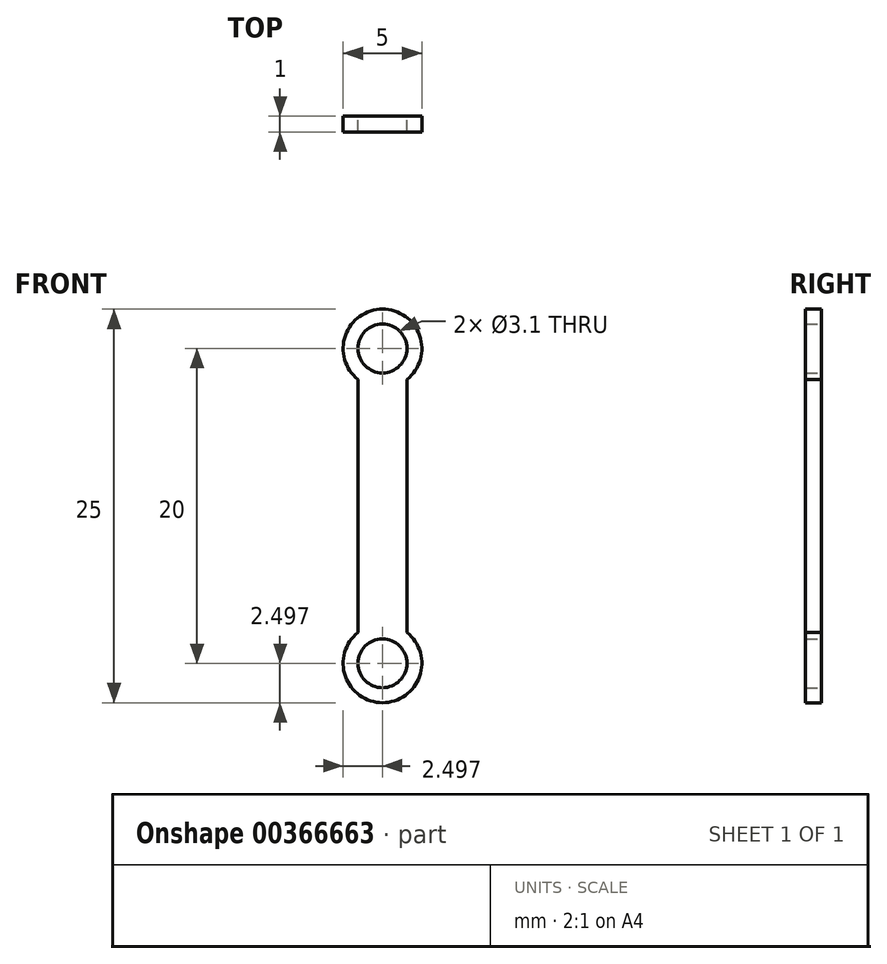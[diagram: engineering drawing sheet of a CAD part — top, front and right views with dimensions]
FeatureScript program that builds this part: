
annotation { "Feature Type Name" : "Feature", "Feature Type Description" : "" }
export const myFeature = defineFeature(function(context is Context, id is Id, definition is map)
    precondition{}
    {
        {
            var Q0;
            Q0=qCreatedBy(makeId("Front.planeOp"),FACE);
            var sketch = newSketch(context, id + "F0", { "sketchPlane" : qUnion([Q0])});
            skCircle(sketch, "E0", {"center": v(12.96, 10.03) * mm, "radius": 1.55 * mm});
            skCircle(sketch, "E1", {"center": v(12.96, 30.03) * mm, "radius": 1.55 * mm});
            skArc(sketch, "E2", {"start": v(14.5, 28.07) * mm, "mid": v(12.96, 32.53) * mm, "end": v(11.4, 28.07) * mm});
            skArc(sketch, "E3", {"start": v(11.4, 11.99) * mm, "mid": v(12.96, 7.53) * mm, "end": v(14.5, 11.99) * mm});
            skLineSegment(sketch, "E4", {"start": v(14.5, 28.07) * mm, "end": v(14.5, 11.99) * mm});
            skLineSegment(sketch, "E5", {"start": v(11.4, 28.07) * mm, "end": v(11.4, 11.99) * mm});
            skSolve(sketch);
        }
        {
            var Q0;
            Q0=makeQuery(id+"F0.imprint","IMPRINT",FACE,{"disambiguationData":[TD([[makeQuery(id+"F0.imprint","IMPRINT",EDGE,{"derivedFrom":sQuery(id+"F0.wireOp",EDGE,"E0")}),-1.0]])]});
            extrude(context, id + "F1", {"entities" : qUnion([Q0]), "depth" : 4.5 * mm});
        }
        {
            var Q0;
            Q0=makeQuery(id+"F1.opExtrude","SWEPT_FACE",FACE,{"disambiguationData":[OSD([sQuery(id+"F0.wireOp",EDGE,"E4")])]});
            var sketch = newSketch(context, id + "F2", { "sketchPlane" : qUnion([Q0])});
            skLineSegment(sketch, "E6.bottom", {"start": v(-1, 33.2) * mm, "end": v(-3.5, 33.2) * mm});
            skLineSegment(sketch, "E6.top", {"start": v(-1, 26.87) * mm, "end": v(-3.5, 26.87) * mm});
            skLineSegment(sketch, "E6.left", {"start": v(-1, 33.2) * mm, "end": v(-1, 26.87) * mm});
            skLineSegment(sketch, "E6.right", {"start": v(-3.5, 33.2) * mm, "end": v(-3.5, 26.87) * mm});
            skSolve(sketch);
        }
        {
            var Q0;
            Q0 = qSketchRegion(id + "F2", true);
            extrude(context, id + "F3", {"entities" : qUnion([Q0]), "operationType" : NewBodyOperationType.REMOVE, "endBound" : BoundingType.THROUGH_ALL, "oppositeDirection" : true, "depth" : 25 * mm, "hasSecondDirection" : true, "secondDirectionBound" : SecondDirectionBoundingType.THROUGH_ALL, "secondDirectionOppositeDirection" : false, "secondDirectionDepth" : 25 * mm});
        }
        {
            var Q0;
            Q0=makeQuery(id+"F1.opExtrude","CAP_FACE",FACE,{"disambiguationData":[OSD([sQuery(id+"F0.wireOp",EDGE,"E0"),sQuery(id+"F0.wireOp",EDGE,"E1"),sQuery(id+"F0.wireOp",EDGE,"E2"),sQuery(id+"F0.wireOp",EDGE,"E3"),sQuery(id+"F0.wireOp",EDGE,"E4"),sQuery(id+"F0.wireOp",EDGE,"E5")])],"isStart":false});
            var sketch = newSketch(context, id + "F4", { "sketchPlane" : qUnion([Q0])});
            skLineSegment(sketch, "E7.bottom", {"start": v(6.41, 36.07) * mm, "end": v(22.17, 36.07) * mm});
            skLineSegment(sketch, "E7.top", {"start": v(6.41, 1.34) * mm, "end": v(22.17, 1.34) * mm});
            skLineSegment(sketch, "E7.left", {"start": v(6.41, 36.07) * mm, "end": v(6.41, 1.34) * mm});
            skLineSegment(sketch, "E7.right", {"start": v(22.17, 36.07) * mm, "end": v(22.17, 1.34) * mm});
            skSolve(sketch);
        }
        {
            var Q0;
            Q0=makeQuery(id+"F4.imprint","IMPRINT",FACE,{"disambiguationData":[TD([[makeQuery(id+"F4.imprint","IMPRINT",EDGE,{"derivedFrom":sQuery(id+"F4.wireOp",EDGE,"E7.bottom")}),-1.0]])]});
            var Q1;
            Q1=makeQuery(id+"F4.imprint","IMPRINT",FACE,{"disambiguationData":[TD([[makeQuery(id+"F4.imprint","IMPRINT",EDGE,{"derivedFrom":makeQuery(id+"F1.opExtrude","CAP_EDGE",EDGE,{"disambiguationData":[OSD([sQuery(id+"F0.wireOp",EDGE,"E0")])],"isStart":false})}),-1.0]])]});
            extrude(context, id + "F5", {"entities" : qUnion([Q0, Q1]), "operationType" : NewBodyOperationType.REMOVE, "oppositeDirection" : true, "depth" : 3.5 * mm});
        }
    });
